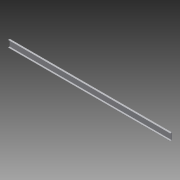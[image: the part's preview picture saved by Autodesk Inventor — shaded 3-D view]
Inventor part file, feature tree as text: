
AUTODESK INVENTOR PART (.ipt)
format: ipt  version: 2013 (Build 170138000, 138)  size: 80,384 bytes
history: native  units: in
note: dims shown in document units (in); Inventor stores cm internally (conversion verified against a paired STEP export)
features: other x2, extrude x1, sketch x1
ambient origin geometry x8: Origin, YZ Plane, XZ Plane, XY Plane, X Axis, Y Axis, Z Axis, Center Point
bodies: Solid1 (feature_tree)
feature tree (4):
  other  "Table"
  other  "Part1-01"
  extrude  "Extrusion1"  Depth=1.0in
  sketch  "Sketch1"  dims[d0=4.0in d1=1.0in d2=0.125in d4=0.0in]
